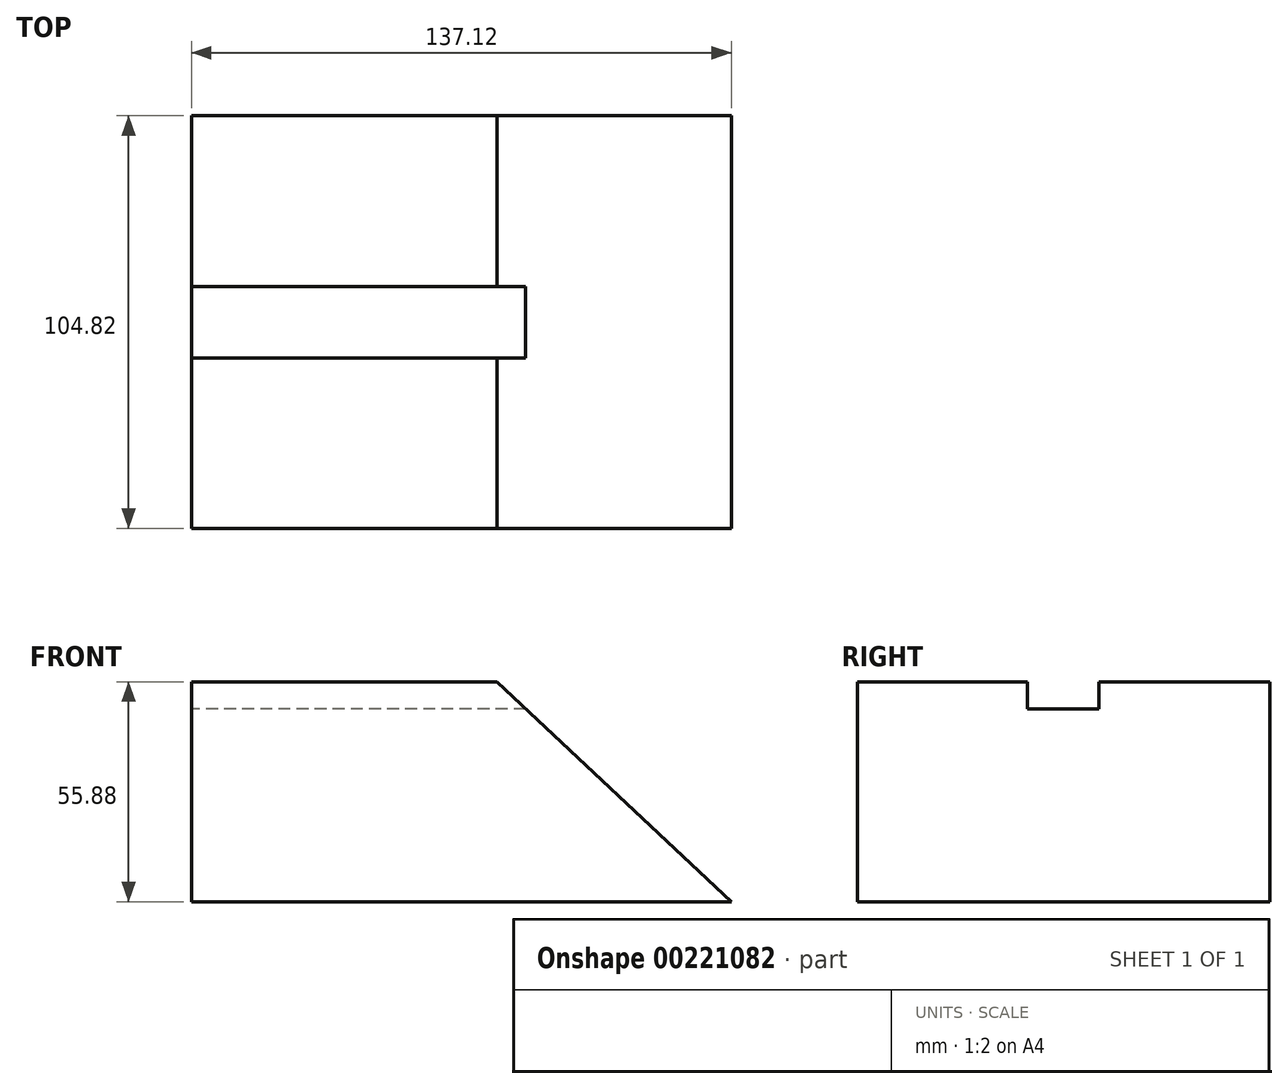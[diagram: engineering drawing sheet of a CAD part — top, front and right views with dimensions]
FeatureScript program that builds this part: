
annotation { "Feature Type Name" : "Feature", "Feature Type Description" : "" }
export const myFeature = defineFeature(function(context is Context, id is Id, definition is map)
    precondition{}
    {
        {
            var Q0;
            Q0=qCreatedBy(makeId("Top.planeOp"),FACE);
            var sketch = newSketch(context, id + "F0", { "sketchPlane" : qUnion([Q0])});
            skLineSegment(sketch, "E0.bottom", {"start": v(68.56, -52.4) * mm, "end": v(-68.56, -52.4) * mm});
            skLineSegment(sketch, "E0.top", {"start": v(68.56, 52.4) * mm, "end": v(-68.56, 52.4) * mm});
            skLineSegment(sketch, "E0.left", {"start": v(68.56, -52.4) * mm, "end": v(68.56, 52.4) * mm});
            skLineSegment(sketch, "E0.right", {"start": v(-68.56, -52.4) * mm, "end": v(-68.56, 52.4) * mm});
            skPoint(sketch, "E0.middle", {"position": v(0, 0) * mm});
            skSolve(sketch);
        }
        {
            var Q0;
            Q0=makeQuery(id+"F0.imprint","IMPRINT",FACE,{"disambiguationData":[TD([[makeQuery(id+"F0.imprint","IMPRINT",EDGE,{"derivedFrom":sQuery(id+"F0.wireOp",EDGE,"E0.bottom")}),-1.0]])]});
            extrude(context, id + "F1", {"entities" : qUnion([Q0]), "depth" : 55.88 * mm});
        }
        {
            var Q0;
            Q0=makeQuery(id+"F1.opExtrude","SWEPT_FACE",FACE,{"disambiguationData":[OSD([sQuery(id+"F0.wireOp",EDGE,"E0.bottom")])]});
            var sketch = newSketch(context, id + "F2", { "sketchPlane" : qUnion([Q0])});
            skLineSegment(sketch, "E1.0", {"start": v(68.56, 55.88) * mm, "end": v(-68.56, 55.88) * mm});
            skLineSegment(sketch, "E2.0", {"start": v(68.56, 55.88) * mm, "end": v(68.56, 0) * mm});
            skLineSegment(sketch, "E3", {"start": v(9.03, 55.88) * mm, "end": v(68.56, 0) * mm});
            skSolve(sketch);
        }
        {
            var Q0;
            Q0 = qSketchRegion(id + "F2", true);
            extrude(context, id + "F3", {"entities" : qUnion([Q0]), "operationType" : NewBodyOperationType.REMOVE, "endBound" : BoundingType.THROUGH_ALL, "oppositeDirection" : true, "depth" : 25.4 * mm});
        }
        {
            var Q0;
            Q0=makeQuery(id+"F1.opExtrude","SWEPT_FACE",FACE,{"disambiguationData":[OSD([sQuery(id+"F0.wireOp",EDGE,"E0.right")])]});
            var sketch = newSketch(context, id + "F4", { "sketchPlane" : qUnion([Q0])});
            skLineSegment(sketch, "E4.0", {"start": v(52.4, 55.88) * mm, "end": v(-52.4, 55.88) * mm});
            skLineSegment(sketch, "E5", {"start": v(-8.99, 55.88) * mm, "end": v(-8.99, 49.04) * mm});
            skLineSegment(sketch, "E6", {"start": v(-8.99, 49.04) * mm, "end": v(9.18, 49.04) * mm});
            skLineSegment(sketch, "E7", {"start": v(9.18, 49.04) * mm, "end": v(9.18, 55.88) * mm});
            skSolve(sketch);
        }
        {
            var Q0;
            Q0 = qSketchRegion(id + "F4", true);
            extrude(context, id + "F5", {"entities" : qUnion([Q0]), "operationType" : NewBodyOperationType.REMOVE, "endBound" : BoundingType.THROUGH_ALL, "oppositeDirection" : true, "depth" : 25.4 * mm});
        }
    });
